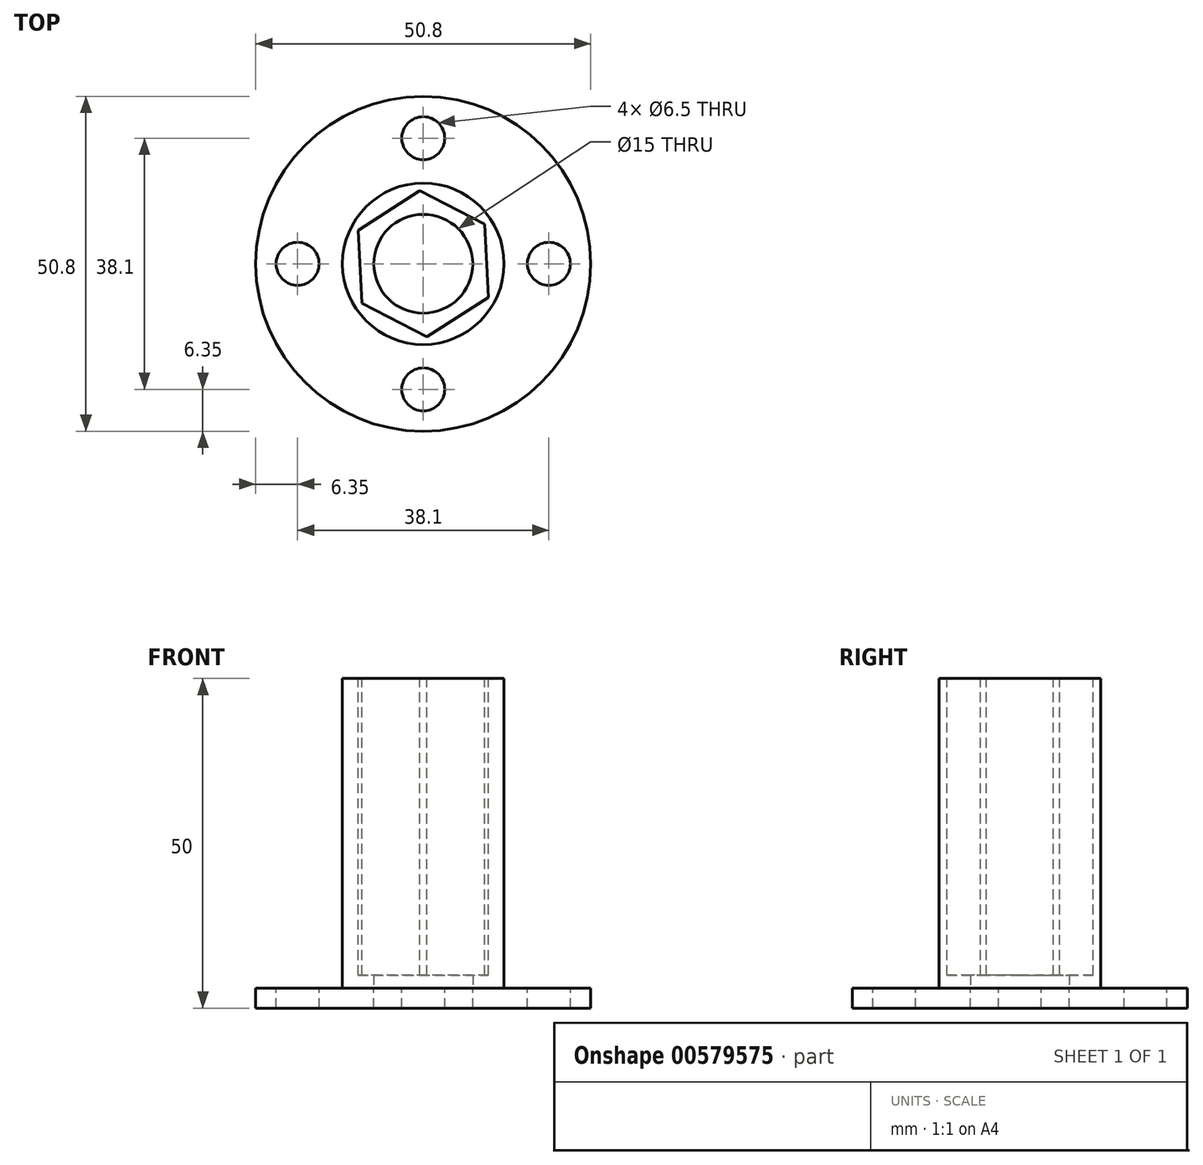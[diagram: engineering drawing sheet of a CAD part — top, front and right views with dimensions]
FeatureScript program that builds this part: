
annotation { "Feature Type Name" : "Feature", "Feature Type Description" : "" }
export const myFeature = defineFeature(function(context is Context, id is Id, definition is map)
    precondition{}
    {
        {
            var Q0;
            Q0=qCreatedBy(makeId("Top.planeOp"),FACE);
            var sketch = newSketch(context, id + "F0", { "sketchPlane" : qUnion([Q0])});
            skCircle(sketch, "E0.cCircle", {"center": v(0, 0) * mm, "radius": 9.6 * mm, "construction": true});
            skLineSegment(sketch, "E0.0", {"start": v(-9.85, 5.08) * mm, "end": v(-0.52, 11.07) * mm});
            skLineSegment(sketch, "E0.1", {"start": v(-0.52, 11.07) * mm, "end": v(9.33, 6) * mm});
            skLineSegment(sketch, "E0.2", {"start": v(9.33, 6) * mm, "end": v(9.85, -5.08) * mm});
            skLineSegment(sketch, "E0.3", {"start": v(9.85, -5.08) * mm, "end": v(0.52, -11.07) * mm});
            skLineSegment(sketch, "E0.4", {"start": v(0.52, -11.07) * mm, "end": v(-9.33, -6) * mm});
            skLineSegment(sketch, "E0.5", {"start": v(-9.33, -6) * mm, "end": v(-9.85, 5.08) * mm});
            skPoint(sketch, "E0.0.midPoint", {"position": v(-5.19, 8.08) * mm});
            skSolve(sketch);
        }
        {
            var Q0;
            Q0=qCreatedBy(makeId("Top.planeOp"),FACE);
            var sketch = newSketch(context, id + "F1", { "sketchPlane" : qUnion([Q0])});
            skCircle(sketch, "E1", {"center": v(0, 0) * mm, "radius": 12.25 * mm});
            skSolve(sketch);
        }
        {
            var Q0;
            Q0=makeQuery(id+"F1.imprint","IMPRINT",FACE,{"disambiguationData":[TD([[makeQuery(id+"F1.imprint","IMPRINT",EDGE,{"derivedFrom":sQuery(id+"F1.wireOp",EDGE,"E1")}),1.0]])]});
            extrude(context, id + "F2", {"entities" : qUnion([Q0]), "oppositeDirection" : true, "depth" : 47 * mm, "offsetDistance" : 25 * mm});
        }
        {
            var Q0;
            Q0=makeQuery(id+"F0.imprint","IMPRINT",FACE,{"disambiguationData":[TD([[makeQuery(id+"F0.imprint","IMPRINT",EDGE,{"derivedFrom":sQuery(id+"F0.wireOp",EDGE,"E0.0")}),-1.0]])]});
            extrude(context, id + "F3", {"entities" : qUnion([Q0]), "operationType" : NewBodyOperationType.REMOVE, "oppositeDirection" : true, "depth" : 45 * mm, "offsetDistance" : 25 * mm});
        }
        {
            var Q0;
            Q0=makeQuery(id+"F2.opExtrude","CAP_FACE",FACE,{"disambiguationData":[OSD([sQuery(id+"F1.wireOp",EDGE,"E1")])],"isStart":false});
            var sketch = newSketch(context, id + "F4", { "sketchPlane" : qUnion([Q0])});
            skCircle(sketch, "E2", {"center": v(0, 0) * mm, "radius": 7.5 * mm});
            skSolve(sketch);
        }
        {
            var Q0;
            Q0=makeQuery(id+"F4.imprint","IMPRINT",FACE,{"disambiguationData":[TD([[makeQuery(id+"F4.imprint","IMPRINT",EDGE,{"derivedFrom":sQuery(id+"F4.wireOp",EDGE,"E2")}),1.0]])]});
            extrude(context, id + "F5", {"entities" : qUnion([Q0]), "operationType" : NewBodyOperationType.REMOVE, "oppositeDirection" : true, "depth" : 25 * mm});
        }
        {
            var Q0;
            Q0=makeQuery(id+"F2.opExtrude","CAP_FACE",FACE,{"disambiguationData":[OSD([sQuery(id+"F1.wireOp",EDGE,"E1")])],"isStart":false});
            var sketch = newSketch(context, id + "F6", { "sketchPlane" : qUnion([Q0])});
            skCircle(sketch, "E3", {"center": v(0, 0) * mm, "radius": 25.4 * mm});
            skPoint(sketch, "E4", {"position": v(0, 19.05) * mm});
            skPoint(sketch, "E5", {"position": v(19.05, 0) * mm});
            skPoint(sketch, "E6", {"position": v(0, -19.05) * mm});
            skPoint(sketch, "E7", {"position": v(-19.05, 0) * mm});
            skCircle(sketch, "E8", {"center": v(0, 19.05) * mm, "radius": 3.25 * mm});
            skCircle(sketch, "E9", {"center": v(19.05, 0) * mm, "radius": 3.25 * mm});
            skCircle(sketch, "E10", {"center": v(0, -19.05) * mm, "radius": 3.25 * mm});
            skCircle(sketch, "E11", {"center": v(-19.05, 0) * mm, "radius": 3.25 * mm});
            skSolve(sketch);
        }
        {
            var Q0;
            Q0=makeQuery(id+"F6.imprint","IMPRINT",FACE,{"disambiguationData":[TD([[makeQuery(id+"F6.imprint","IMPRINT",EDGE,{"derivedFrom":sQuery(id+"F6.wireOp",EDGE,"E3")}),1.0]])]});
            var Q1;
            Q1=makeQuery(id+"F6.imprint","IMPRINT",FACE,{"disambiguationData":[TD([[makeQuery(id+"F6.imprint","IMPRINT",EDGE,{"derivedFrom":makeQuery(id+"F2.opExtrude","CAP_EDGE",EDGE,{"disambiguationData":[OSD([sQuery(id+"F1.wireOp",EDGE,"E1")])],"isStart":false})}),-1.0]])]});
            extrude(context, id + "F7", {"entities" : qUnion([Q0, Q1]), "depth" : 3 * mm, "offsetDistance" : 25 * mm});
        }
    });
